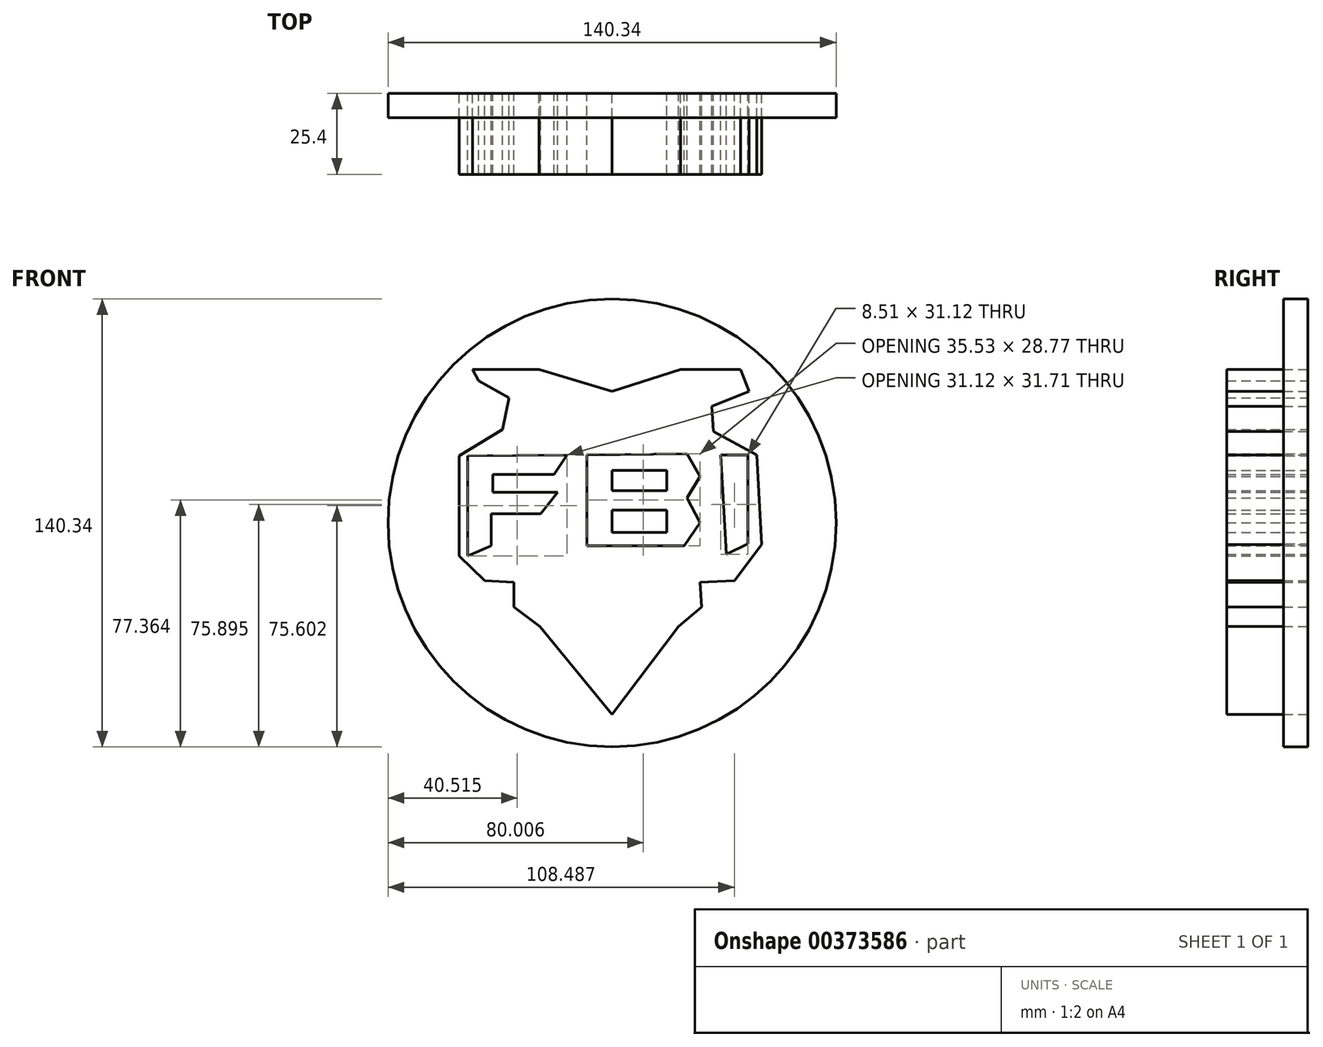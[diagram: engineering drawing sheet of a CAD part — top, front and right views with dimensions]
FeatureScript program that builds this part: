
annotation { "Feature Type Name" : "Feature", "Feature Type Description" : "" }
export const myFeature = defineFeature(function(context is Context, id is Id, definition is map)
    precondition{}
    {
        {
            var Q0;
            Q0=qCreatedBy(makeId("Front.planeOp"),FACE);
            var sketch = newSketch(context, id + "F0", { "sketchPlane" : qUnion([Q0])});
            skLineSegment(sketch, "E0", {"start": v(-14.1, 21.29) * mm, "end": v(-18.2, 15.12) * mm});
            skLineSegment(sketch, "E1", {"start": v(-18.2, 15.12) * mm, "end": v(-37.29, 15.12) * mm});
            skLineSegment(sketch, "E2", {"start": v(-37.29, 15.12) * mm, "end": v(-37.29, 9.54) * mm});
            skLineSegment(sketch, "E3", {"start": v(-37.29, 9.54) * mm, "end": v(-17.03, 9.54) * mm});
            skLineSegment(sketch, "E4", {"start": v(-17.03, 9.54) * mm, "end": v(-22.31, 2.79) * mm});
            skLineSegment(sketch, "E5", {"start": v(-22.31, 2.79) * mm, "end": v(-37.88, 2.79) * mm});
            skLineSegment(sketch, "E6", {"start": v(-37.88, 2.79) * mm, "end": v(-37.88, -7.2) * mm});
            skLineSegment(sketch, "E7", {"start": v(-37.88, -7.2) * mm, "end": v(-45.22, -10.42) * mm});
            skLineSegment(sketch, "E8", {"start": v(-45.22, -10.42) * mm, "end": v(-45.22, 21) * mm});
            skLineSegment(sketch, "E9", {"start": v(-45.22, 21) * mm, "end": v(-14.1, 21.29) * mm});
            skLineSegment(sketch, "E10", {"start": v(-7.93, 21.29) * mm, "end": v(-7.93, -7.2) * mm});
            skLineSegment(sketch, "E11", {"start": v(-7.93, -7.2) * mm, "end": v(22.6, -7.2) * mm});
            skLineSegment(sketch, "E12", {"start": v(22.6, -7.2) * mm, "end": v(27.6, 0) * mm});
            skLineSegment(sketch, "E13", {"start": v(27.6, 0) * mm, "end": v(23.49, 7.78) * mm});
            skLineSegment(sketch, "E14", {"start": v(23.49, 7.78) * mm, "end": v(27.6, 14.53) * mm});
            skLineSegment(sketch, "E15", {"start": v(27.6, 14.53) * mm, "end": v(23.49, 21.58) * mm});
            skLineSegment(sketch, "E16", {"start": v(23.49, 21.58) * mm, "end": v(-7.93, 21.29) * mm});
            skLineSegment(sketch, "E17", {"start": v(34.06, 21.29) * mm, "end": v(42.57, 21.29) * mm});
            skLineSegment(sketch, "E18", {"start": v(42.57, 21.29) * mm, "end": v(42.57, -6.6) * mm});
            skLineSegment(sketch, "E19", {"start": v(42.57, -6.6) * mm, "end": v(35.82, -9.84) * mm});
            skLineSegment(sketch, "E20", {"start": v(35.82, -9.84) * mm, "end": v(34.06, 21.29) * mm});
            skLineSegment(sketch, "E21", {"start": v(-32.3, 39.2) * mm, "end": v(-16.15, 40.11) * mm});
            skPoint(sketch, "E21.endSnap0", {"position": v(-16.15, 18.2) * mm});
            skLineSegment(sketch, "E22", {"start": v(-16.15, 40.11) * mm, "end": v(-2.92, 31.3) * mm});
            skLineSegment(sketch, "E23", {"start": v(-2.92, 31.3) * mm, "end": v(16.44, 39.2) * mm});
            skLineSegment(sketch, "E24", {"start": v(16.44, 39.2) * mm, "end": v(31.06, 40.02) * mm});
            skLineSegment(sketch, "E25", {"start": v(31.06, 40.02) * mm, "end": v(31.7, 28.63) * mm});
            skLineSegment(sketch, "E26", {"start": v(38.32, -18.06) * mm, "end": v(27.6, -18.66) * mm});
            skLineSegment(sketch, "E27", {"start": v(27.6, -18.66) * mm, "end": v(28.03, -26.34) * mm});
            skLineSegment(sketch, "E28", {"start": v(28.03, -26.34) * mm, "end": v(20.85, -32.44) * mm});
            skLineSegment(sketch, "E29", {"start": v(20.85, -32.44) * mm, "end": v(0, -60.04) * mm});
            skLineSegment(sketch, "E30", {"start": v(0, -60.04) * mm, "end": v(-22.6, -32.44) * mm});
            skLineSegment(sketch, "E31", {"start": v(-22.6, -32.44) * mm, "end": v(-30.7, -26.34) * mm});
            skLineSegment(sketch, "E32", {"start": v(-30.7, -26.34) * mm, "end": v(-30.7, -18.66) * mm});
            skLineSegment(sketch, "E33", {"start": v(-30.7, -18.66) * mm, "end": v(-39.93, -18.06) * mm});
            skLineSegment(sketch, "E34", {"start": v(-56.67, 6.02) * mm, "end": v(-56.67, 10.13) * mm});
            skLineSegment(sketch, "E35", {"start": v(-9.53, 35.7) * mm, "end": v(0, 41.25) * mm});
            skLineSegment(sketch, "E36", {"start": v(0, 41.25) * mm, "end": v(4.12, 34.17) * mm});
            skLineSegment(sketch, "E37", {"start": v(0, 41.25) * mm, "end": v(21.43, 48) * mm});
            skLineSegment(sketch, "E38", {"start": v(21.43, 48) * mm, "end": v(40.23, 48) * mm});
            skLineSegment(sketch, "E39", {"start": v(40.23, 48) * mm, "end": v(42.98, 41.25) * mm});
            skLineSegment(sketch, "E40", {"start": v(42.98, 41.25) * mm, "end": v(31.26, 36.47) * mm});
            skLineSegment(sketch, "E41", {"start": v(0, 41.25) * mm, "end": v(-22.9, 48) * mm});
            skLineSegment(sketch, "E42", {"start": v(-22.9, 48) * mm, "end": v(-43.75, 48) * mm});
            skLineSegment(sketch, "E43", {"start": v(-43.75, 48) * mm, "end": v(-41.74, 44.55) * mm});
            skLineSegment(sketch, "E44", {"start": v(-41.74, 44.55) * mm, "end": v(-32.3, 39.2) * mm});
            skLineSegment(sketch, "E45", {"start": v(-32.3, 2.79) * mm, "end": v(-32.3, -11.01) * mm});
            skLineSegment(sketch, "E46", {"start": v(-32.3, -11.01) * mm, "end": v(-18.5, -13.95) * mm});
            skLineSegment(sketch, "E47", {"start": v(-18.5, -13.95) * mm, "end": v(-2.1, -40.63) * mm});
            skLineSegment(sketch, "E48", {"start": v(-2.1, -40.63) * mm, "end": v(15.68, -13.95) * mm});
            skLineSegment(sketch, "E49", {"start": v(15.68, -13.95) * mm, "end": v(31.26, -10.42) * mm});
            skLineSegment(sketch, "E50", {"start": v(31.26, -10.42) * mm, "end": v(34.46, 14.26) * mm});
            skLineSegment(sketch, "E51", {"start": v(0, 15.1) * mm, "end": v(16.63, 15.1) * mm});
            skLineSegment(sketch, "E52", {"start": v(16.63, 15.1) * mm, "end": v(20.58, 13.12) * mm});
            skLineSegment(sketch, "E53", {"start": v(20.58, 13.12) * mm, "end": v(17.62, 9.66) * mm});
            skLineSegment(sketch, "E54", {"start": v(17.62, 9.66) * mm, "end": v(0, 9.66) * mm});
            skLineSegment(sketch, "E55", {"start": v(0, 9.66) * mm, "end": v(0, 15.1) * mm});
            skLineSegment(sketch, "E56", {"start": v(0, 4.23) * mm, "end": v(0, 0) * mm});
            skLineSegment(sketch, "E57", {"start": v(0, 0) * mm, "end": v(17.13, 0) * mm});
            skLineSegment(sketch, "E58", {"start": v(17.13, 0) * mm, "end": v(17.13, 5.22) * mm});
            skLineSegment(sketch, "E59", {"start": v(17.13, 5.22) * mm, "end": v(0, 4.23) * mm});
            skLineSegment(sketch, "E60", {"start": v(-45.22, 21) * mm, "end": v(-45.22, 19.49) * mm});
            skLineSegment(sketch, "E61", {"start": v(-47.9, 21) * mm, "end": v(-47.9, -10.4) * mm});
            skLineSegment(sketch, "E62", {"start": v(-47.9, 21) * mm, "end": v(-34.34, 29.32) * mm});
            skLineSegment(sketch, "E63", {"start": v(-34.34, 29.32) * mm, "end": v(-32.3, 39.2) * mm});
            skLineSegment(sketch, "E64", {"start": v(31.7, 28.63) * mm, "end": v(45.33, 21.29) * mm});
            skLineSegment(sketch, "E65", {"start": v(45.33, 21.29) * mm, "end": v(46.92, -6.82) * mm});
            skLineSegment(sketch, "E66", {"start": v(46.92, -6.82) * mm, "end": v(38.32, -18.06) * mm});
            skLineSegment(sketch, "E67", {"start": v(-47.9, -10.4) * mm, "end": v(-39.93, -18.06) * mm});
            skLineSegment(sketch, "E68", {"start": v(0, 15.1) * mm, "end": v(-7.93, 21.29) * mm});
            skLineSegment(sketch, "E69", {"start": v(16.63, 15.1) * mm, "end": v(23.49, 21.58) * mm});
            skLineSegment(sketch, "E70", {"start": v(17.62, 9.66) * mm, "end": v(23.49, 7.78) * mm});
            skLineSegment(sketch, "E71", {"start": v(0, 9.66) * mm, "end": v(-7.93, 7.78) * mm});
            skLineSegment(sketch, "E72", {"start": v(0, 4.23) * mm, "end": v(-7.93, 7.78) * mm});
            skLineSegment(sketch, "E73", {"start": v(0, 0) * mm, "end": v(-7.93, -7.2) * mm});
            skLineSegment(sketch, "E74", {"start": v(17.13, 0) * mm, "end": v(22.6, -7.2) * mm});
            skLineSegment(sketch, "E75", {"start": v(17.2, 6) * mm, "end": v(23.49, 7.78) * mm});
            skCircle(sketch, "E76", {"center": v(0, 0) * mm, "radius": 72.84 * mm});
            skSolve(sketch);
        }
        {
            var Q0;
            {var subQ2=sQuery(id+"F0.wireOp",EDGE,"E21");Q0=makeQuery(id+"F0.imprint","IMPRINT",FACE,{"disambiguationData":[TD([[makeQuery(id+"F0.imprint","IMPRINT",EDGE,{"derivedFrom":subQ2}),1.0]])]});}
            var Q1;
            {var subQ2=sQuery(id+"F0.wireOp",EDGE,"E24");Q1=makeQuery(id+"F0.imprint","IMPRINT",FACE,{"disambiguationData":[TD([[makeQuery(id+"F0.imprint","IMPRINT",EDGE,{"derivedFrom":subQ2}),1.0]])]});}
            var Q2;
            {var subQ3=sQuery(id+"F0.wireOp",EDGE,"E6");Q2=makeQuery(id+"F0.imprint","IMPRINT",FACE,{"disambiguationData":[TD([[makeQuery(id+"F0.imprint","IMPRINT",EDGE,{"derivedFrom":subQ3}),1.0]])]});}
            var Q3;
            {var subQ3=sQuery(id+"F0.wireOp",EDGE,"E35");Q3=makeQuery(id+"F0.imprint","IMPRINT",FACE,{"disambiguationData":[TD([[makeQuery(id+"F0.imprint","IMPRINT",EDGE,{"derivedFrom":subQ3}),-1.0]])]});}
            var Q4;
            Q4=makeQuery(id+"F0.imprint","IMPRINT",FACE,{"disambiguationData":[TD([[makeQuery(id+"F0.imprint","IMPRINT",EDGE,{"derivedFrom":sQuery(id+"F0.wireOp",EDGE,"E0")}),1.0]])]});
            extrude(context, id + "F1", {"entities" : qUnion([Q0, Q1, Q2, Q3, Q4]), "depth" : 25.4 * mm});
        }
        {
            var Q0;
            Q0=qCreatedBy(makeId("Front.planeOp"),FACE);
            var sketch = newSketch(context, id + "F2", { "sketchPlane" : qUnion([Q0])});
            skLineSegment(sketch, "E77.bottom", {"start": v(0, 16.46) * mm, "end": v(17.2, 16.46) * mm});
            skLineSegment(sketch, "E77.top", {"start": v(0, 10.07) * mm, "end": v(17.2, 10.07) * mm});
            skLineSegment(sketch, "E77.left", {"start": v(0, 16.46) * mm, "end": v(0, 10.07) * mm});
            skLineSegment(sketch, "E77.right", {"start": v(17.2, 16.46) * mm, "end": v(17.2, 10.07) * mm});
            skLineSegment(sketch, "E78.bottom", {"start": v(0, 3.98) * mm, "end": v(17.2, 3.98) * mm});
            skLineSegment(sketch, "E78.top", {"start": v(0, -3) * mm, "end": v(17.2, -3) * mm});
            skLineSegment(sketch, "E78.left", {"start": v(0, 3.98) * mm, "end": v(0, -3) * mm});
            skLineSegment(sketch, "E78.right", {"start": v(17.2, 3.98) * mm, "end": v(17.2, -3) * mm});
            skSolve(sketch);
        }
        {
            var Q0;
            Q0 = qSketchRegion(id + "F2", true);
            extrude(context, id + "F3", {"entities" : qUnion([Q0]), "depth" : 25.4 * mm});
        }
        {
            var Q0;
            Q0=qCreatedBy(makeId("Front.planeOp"),FACE);
            var sketch = newSketch(context, id + "F4", { "sketchPlane" : qUnion([Q0])});
            skCircle(sketch, "E79", {"center": v(0, 0) * mm, "radius": 70.17 * mm});
            skSolve(sketch);
        }
        {
            var Q0;
            Q0 = qSketchRegion(id + "F4", true);
            extrude(context, id + "F5", {"entities" : qUnion([Q0]), "depth" : 7.62 * mm});
        }
    });
